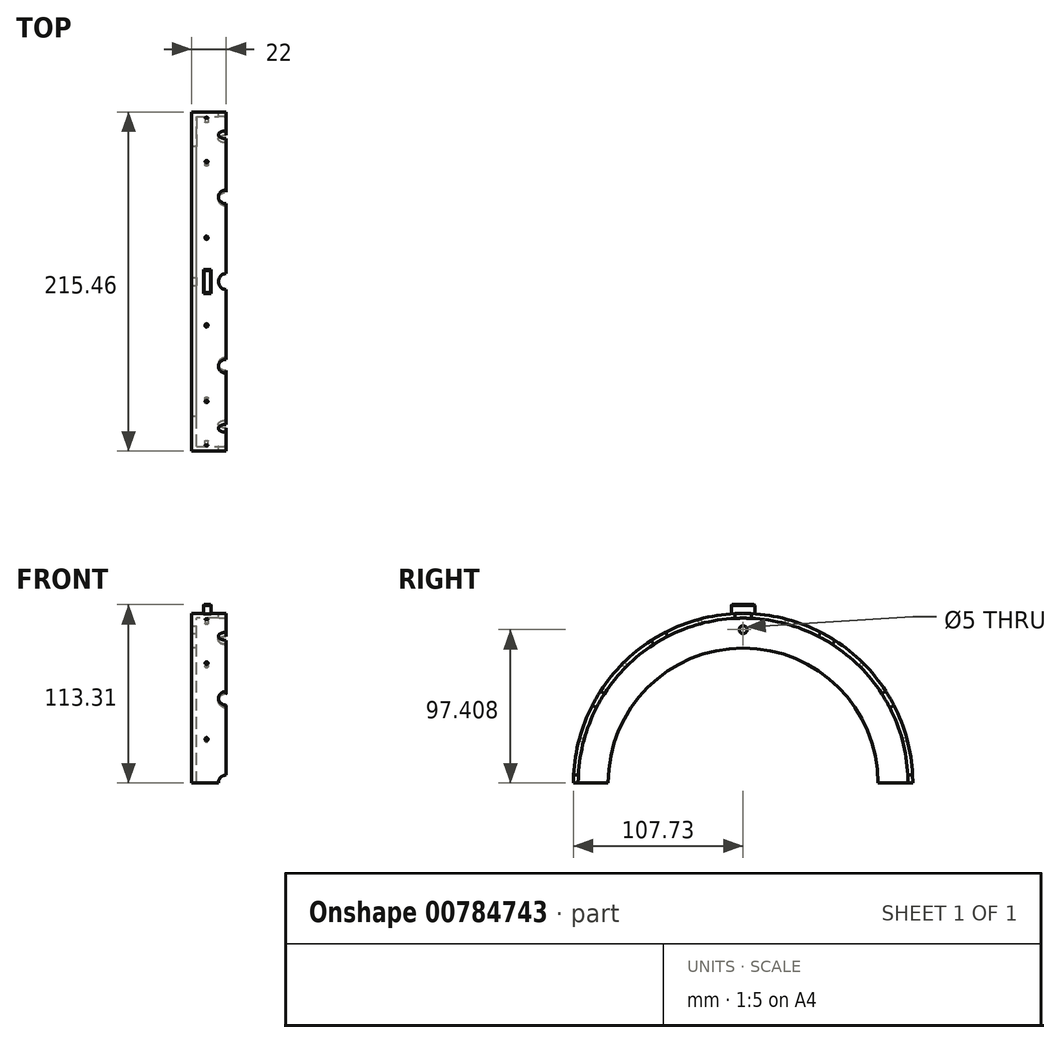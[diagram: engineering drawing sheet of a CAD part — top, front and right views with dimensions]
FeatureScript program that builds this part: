
annotation { "Feature Type Name" : "Feature", "Feature Type Description" : "" }
export const myFeature = defineFeature(function(context is Context, id is Id, definition is map)
    precondition{}
    {
        {
            var Q0;
            Q0=qCreatedBy(makeId("Top.planeOp"),FACE);
            var sketch = newSketch(context, id + "F0", { "sketchPlane" : qUnion([Q0])});
            skLineSegment(sketch, "E0", {"start": v(-37.45, 0) * mm, "end": v(31.85, 0) * mm, "construction": true});
            skLineSegment(sketch, "E1", {"start": v(-6.93, 104.73) * mm, "end": v(-6.93, 85.73) * mm});
            skLineSegment(sketch, "E2", {"start": v(-6.93, 85.73) * mm, "end": v(-9.93, 85.73) * mm});
            skLineSegment(sketch, "E3", {"start": v(-9.93, 85.73) * mm, "end": v(-9.93, 107.73) * mm});
            skLineSegment(sketch, "E4", {"start": v(-6.93, 104.73) * mm, "end": v(9.07, 104.73) * mm});
            skLineSegment(sketch, "E5", {"start": v(12.07, 107.73) * mm, "end": v(12.07, 104.73) * mm});
            skLineSegment(sketch, "E6", {"start": v(-9.93, 107.73) * mm, "end": v(12.07, 107.73) * mm});
            skLineSegment(sketch, "E7.trimOffspring", {"start": v(10.07, 104.73) * mm, "end": v(12.07, 104.73) * mm});
            skLineSegment(sketch, "E8", {"start": v(9.07, 104.73) * mm, "end": v(10.07, 104.73) * mm});
            skSolve(sketch);
        }
        {
            var Q0;
            Q0=qSketchRegion(id+"F0",true);
            var Q1;
            Q1=sQuery(id+"F0.wireOp",EDGE,"E0");
            revolve(context, id + "F1", {"surfaceOperationType" : NewSurfaceOperationType.NEW, "entities" : qUnion([Q0]), "axis" : qUnion([Q1]), "revolveType" : RevolveType.ONE_DIRECTION, "angle" : 180 * degree});
        }
        {
            var Q0;
            Q0=qCreatedBy(makeId("Right.planeOp"),FACE);
            var sketch = newSketch(context, id + "F2", { "sketchPlane" : qUnion([Q0])});
            skLineSegment(sketch, "E9", {"start": v(0, 0) * mm, "end": v(61.84, 107.11) * mm, "construction": true});
            skLineSegment(sketch, "E10", {"start": v(0, 0) * mm, "end": v(0, 110.2) * mm, "construction": true});
            skLineSegment(sketch, "E11", {"start": v(0, 0) * mm, "end": v(-59.27, 102.65) * mm, "construction": true});
            skLineSegment(sketch, "E12", {"start": v(0, 0) * mm, "end": v(108.53, 62.66) * mm, "construction": true});
            skLineSegment(sketch, "E13", {"start": v(0, 0) * mm, "end": v(-111.98, 64.65) * mm, "construction": true});
            skLineSegment(sketch, "E14", {"start": v(0, 0) * mm, "end": v(-132.1, 0) * mm, "construction": true});
            skLineSegment(sketch, "E15", {"start": v(0, 0) * mm, "end": v(126.53, 0) * mm, "construction": true});
            skPoint(sketch, "E16", {"position": v(-59.27, 102.65) * mm});
            skPoint(sketch, "E17", {"position": v(-111.98, 64.65) * mm});
            skPoint(sketch, "E18", {"position": v(-132.1, 0) * mm});
            skPoint(sketch, "E19", {"position": v(0, 110.2) * mm});
            skPoint(sketch, "E20", {"position": v(61.84, 107.11) * mm});
            skPoint(sketch, "E21", {"position": v(108.53, 62.66) * mm});
            skPoint(sketch, "E22", {"position": v(126.53, 0) * mm});
            skLineSegment(sketch, "E23", {"start": v(0, 0) * mm, "end": v(-120.74, 32.35) * mm, "construction": true});
            skLineSegment(sketch, "E24.MirrorCS", {"start": v(0, 0) * mm, "end": v(-88.39, 88.39) * mm, "construction": true});
            skLineSegment(sketch, "E25.MirrorCS", {"start": v(0, 0) * mm, "end": v(-32.35, 120.74) * mm, "construction": true});
            skLineSegment(sketch, "E26.MirrorCS", {"start": v(0, 0) * mm, "end": v(32.35, 120.74) * mm, "construction": true});
            skLineSegment(sketch, "E27.MirrorCS", {"start": v(0, 0) * mm, "end": v(88.39, 88.39) * mm, "construction": true});
            skLineSegment(sketch, "E28.MirrorCS", {"start": v(0, 0) * mm, "end": v(120.74, 32.35) * mm, "construction": true});
            skSolve(sketch);
        }
        {
            var Q0;
            Q0=qCreatedBy(makeId("Front.planeOp"),FACE);
            var Q1;
            Q1=sQuery(id+"F2.wireOp",EDGE,"E13");
            cPlane(context, id + "F3", {"entities" : qUnion([Q0, Q1]), "cplaneType" : CPlaneType.LINE_ANGLE, "offset" : 25 * mm, "angle" : 0 * degree, "width" : 150 * mm, "height" : 150 * mm});
        }
        {
            var Q0;
            Q0=qCreatedBy(id+"F3.planeOp",FACE);
            var sketch = newSketch(context, id + "F4", { "sketchPlane" : qUnion([Q0])});
            skArc(sketch, "E29", {"start": v(12.07, -113.43) * mm, "mid": v(17.27, -105.94) * mm, "end": v(12.07, -98.44) * mm});
            skLineSegment(sketch, "E30", {"start": v(12.07, -113.43) * mm, "end": v(12.07, -98.44) * mm});
            skSolve(sketch);
        }
        {
            var Q0;
            Q0=qSketchRegion(id+"F4",true);
            var Q1;
            Q1=sQuery(id+"F4.wireOp",EDGE,"E30");
            revolve(context, id + "F5", {"operationType" : NewBodyOperationType.REMOVE, "surfaceOperationType" : NewSurfaceOperationType.NEW, "entities" : qUnion([Q0]), "axis" : qUnion([Q1]), "revolveType" : RevolveType.FULL, "oppositeDirection" : true});
        }
        {
            var Q0;
            Q0=sQuery(id+"F2.wireOp",EDGE,"E11");
            cPlane(context, id + "F6", {"entities" : qUnion([Q0]), "cplaneType" : CPlaneType.LINE_ANGLE, "offset" : 25 * mm, "angle" : 90 * degree, "width" : 150 * mm, "height" : 150 * mm});
        }
        {
            var Q0;
            Q0=qCreatedBy(id+"F6.planeOp",FACE);
            var sketch = newSketch(context, id + "F7", { "sketchPlane" : qUnion([Q0])});
            skArc(sketch, "E31", {"start": v(-12.1, 98.77) * mm, "mid": v(-6.9, 106.26) * mm, "end": v(-12.1, 113.76) * mm});
            skLineSegment(sketch, "E32", {"start": v(-12.1, 98.77) * mm, "end": v(-12.1, 113.76) * mm});
            skSolve(sketch);
        }
        {
            var Q0;
            Q0=qSketchRegion(id+"F7",true);
            var Q1;
            Q1=sQuery(id+"F7.wireOp",EDGE,"E32");
            revolve(context, id + "F8", {"operationType" : NewBodyOperationType.REMOVE, "surfaceOperationType" : NewSurfaceOperationType.NEW, "entities" : qUnion([Q0]), "axis" : qUnion([Q1]), "revolveType" : RevolveType.FULL, "oppositeDirection" : true});
        }
        {
            var Q0;
            Q0=sQuery(id+"F2.wireOp",EDGE,"E10");
            cPlane(context, id + "F9", {"entities" : qUnion([Q0]), "cplaneType" : CPlaneType.LINE_ANGLE, "offset" : 25 * mm, "angle" : 90 * degree, "width" : 150 * mm, "height" : 150 * mm});
        }
        {
            var Q0;
            Q0=qCreatedBy(id+"F9.planeOp",FACE);
            var sketch = newSketch(context, id + "F10", { "sketchPlane" : qUnion([Q0])});
            skArc(sketch, "E33", {"start": v(-12.07, 98.66) * mm, "mid": v(-6.87, 106.16) * mm, "end": v(-12.07, 113.65) * mm});
            skLineSegment(sketch, "E34", {"start": v(-12.07, 98.66) * mm, "end": v(-12.07, 113.65) * mm});
            skSolve(sketch);
        }
        {
            var Q0;
            Q0=qSketchRegion(id+"F10",true);
            var Q1;
            Q1=sQuery(id+"F10.wireOp",EDGE,"E34");
            revolve(context, id + "F11", {"operationType" : NewBodyOperationType.REMOVE, "surfaceOperationType" : NewSurfaceOperationType.NEW, "entities" : qUnion([Q0]), "axis" : qUnion([Q1]), "revolveType" : RevolveType.FULL, "oppositeDirection" : true});
        }
        {
            var Q0;
            Q0=sQuery(id+"F2.wireOp",EDGE,"E9");
            cPlane(context, id + "F12", {"entities" : qUnion([Q0]), "cplaneType" : CPlaneType.LINE_ANGLE, "offset" : 25 * mm, "angle" : 90 * degree, "width" : 150 * mm, "height" : 150 * mm});
        }
        {
            var Q0;
            Q0=qCreatedBy(id+"F12.planeOp",FACE);
            var sketch = newSketch(context, id + "F13", { "sketchPlane" : qUnion([Q0])});
            skArc(sketch, "E35", {"start": v(-12.07, 98.61) * mm, "mid": v(-6.87, 106.1) * mm, "end": v(-12.07, 113.6) * mm});
            skLineSegment(sketch, "E36", {"start": v(-12.07, 98.61) * mm, "end": v(-12.07, 113.6) * mm});
            skSolve(sketch);
        }
        {
            var Q0;
            Q0=qSketchRegion(id+"F13",true);
            var Q1;
            Q1=sQuery(id+"F13.wireOp",EDGE,"E36");
            revolve(context, id + "F14", {"operationType" : NewBodyOperationType.REMOVE, "surfaceOperationType" : NewSurfaceOperationType.NEW, "entities" : qUnion([Q0]), "axis" : qUnion([Q1]), "revolveType" : RevolveType.FULL, "oppositeDirection" : true});
        }
        {
            var Q0;
            Q0=sQuery(id+"F2.wireOp",EDGE,"E12");
            cPlane(context, id + "F15", {"entities" : qUnion([Q0]), "cplaneType" : CPlaneType.LINE_ANGLE, "offset" : 25 * mm, "angle" : 0 * degree, "width" : 150 * mm, "height" : 150 * mm});
        }
        {
            var Q0;
            Q0=qCreatedBy(id+"F15.planeOp",FACE);
            var sketch = newSketch(context, id + "F16", { "sketchPlane" : qUnion([Q0])});
            skArc(sketch, "E37", {"start": v(12.07, 98.66) * mm, "mid": v(17.27, 106.16) * mm, "end": v(12.07, 113.65) * mm});
            skLineSegment(sketch, "E38", {"start": v(12.07, 98.66) * mm, "end": v(12.07, 113.65) * mm});
            skSolve(sketch);
        }
        {
            var Q0;
            Q0=qSketchRegion(id+"F16",true);
            var Q1;
            Q1=sQuery(id+"F16.wireOp",EDGE,"E38");
            revolve(context, id + "F17", {"operationType" : NewBodyOperationType.REMOVE, "surfaceOperationType" : NewSurfaceOperationType.NEW, "entities" : qUnion([Q0]), "axis" : qUnion([Q1]), "revolveType" : RevolveType.FULL, "oppositeDirection" : true});
        }
        {
            var Q0;
            Q0=sQuery(id+"F2.wireOp",EDGE,"E23");
            cPlane(context, id + "F18", {"entities" : qUnion([Q0]), "cplaneType" : CPlaneType.LINE_ANGLE, "offset" : 25 * mm, "angle" : 0 * degree, "width" : 150 * mm, "height" : 150 * mm});
        }
        {
            var Q0;
            Q0=sQuery(id+"F2.wireOp",EDGE,"E24.MirrorCS");
            cPlane(context, id + "F19", {"entities" : qUnion([Q0]), "cplaneType" : CPlaneType.LINE_ANGLE, "offset" : 25 * mm, "angle" : 0 * degree, "width" : 150 * mm, "height" : 150 * mm});
        }
        {
            var Q0;
            Q0=sQuery(id+"F2.wireOp",EDGE,"E25.MirrorCS");
            cPlane(context, id + "F20", {"entities" : qUnion([Q0]), "cplaneType" : CPlaneType.LINE_ANGLE, "offset" : 25 * mm, "angle" : 90 * degree, "width" : 150 * mm, "height" : 150 * mm});
        }
        {
            var Q0;
            Q0=sQuery(id+"F2.wireOp",EDGE,"E26.MirrorCS");
            cPlane(context, id + "F21", {"entities" : qUnion([Q0]), "cplaneType" : CPlaneType.LINE_ANGLE, "offset" : 25 * mm, "angle" : 90 * degree, "width" : 150 * mm, "height" : 150 * mm});
        }
        {
            var Q0;
            Q0=sQuery(id+"F2.wireOp",EDGE,"E27.MirrorCS");
            cPlane(context, id + "F22", {"entities" : qUnion([Q0]), "cplaneType" : CPlaneType.LINE_ANGLE, "offset" : 25 * mm, "angle" : 0 * degree, "width" : 150 * mm, "height" : 150 * mm});
        }
        {
            var Q0;
            Q0=sQuery(id+"F2.wireOp",EDGE,"E28.MirrorCS");
            cPlane(context, id + "F23", {"entities" : qUnion([Q0]), "cplaneType" : CPlaneType.LINE_ANGLE, "offset" : 25 * mm, "angle" : 0 * degree, "width" : 150 * mm, "height" : 150 * mm});
        }
        {
            var Q0;
            Q0=qCreatedBy(id+"F18.planeOp",FACE);
            var sketch = newSketch(context, id + "F24", { "sketchPlane" : qUnion([Q0])});
            skLineSegment(sketch, "E39.bottom", {"start": v(-1.5, 110.33) * mm, "end": v(-0.5, 110.33) * mm});
            skLineSegment(sketch, "E39.top", {"start": v(-1.5, 102.33) * mm, "end": v(-0.5, 102.33) * mm});
            skLineSegment(sketch, "E39.left", {"start": v(-1.5, 110.33) * mm, "end": v(-1.5, 102.33) * mm});
            skLineSegment(sketch, "E39.right", {"start": v(-0.5, 110.33) * mm, "end": v(-0.5, 102.33) * mm});
            skSolve(sketch);
        }
        {
            var Q0;
            Q0=qSketchRegion(id+"F24",true);
            var Q1;
            Q1=sQuery(id+"F24.wireOp",EDGE,"E39.right");
            revolve(context, id + "F25", {"operationType" : NewBodyOperationType.REMOVE, "surfaceOperationType" : NewSurfaceOperationType.NEW, "entities" : qUnion([Q0]), "axis" : qUnion([Q1]), "revolveType" : RevolveType.FULL, "oppositeDirection" : true});
        }
        {
            var Q0;
            Q0=qCreatedBy(id+"F19.planeOp",FACE);
            var sketch = newSketch(context, id + "F26", { "sketchPlane" : qUnion([Q0])});
            skLineSegment(sketch, "E40.bottom", {"start": v(-1.5, 111.6) * mm, "end": v(-0.5, 111.6) * mm});
            skLineSegment(sketch, "E40.top", {"start": v(-1.5, 103.6) * mm, "end": v(-0.5, 103.6) * mm});
            skLineSegment(sketch, "E40.left", {"start": v(-1.5, 111.6) * mm, "end": v(-1.5, 103.6) * mm});
            skLineSegment(sketch, "E40.right", {"start": v(-0.5, 111.6) * mm, "end": v(-0.5, 103.6) * mm});
            skSolve(sketch);
        }
        {
            var Q0;
            Q0=qSketchRegion(id+"F26",true);
            var Q1;
            Q1=sQuery(id+"F26.wireOp",EDGE,"E40.right");
            revolve(context, id + "F27", {"operationType" : NewBodyOperationType.REMOVE, "surfaceOperationType" : NewSurfaceOperationType.NEW, "entities" : qUnion([Q0]), "axis" : qUnion([Q1]), "revolveType" : RevolveType.FULL, "oppositeDirection" : true});
        }
        {
            var Q0;
            Q0=qCreatedBy(id+"F20.planeOp",FACE);
            var sketch = newSketch(context, id + "F28", { "sketchPlane" : qUnion([Q0])});
            skLineSegment(sketch, "E41.bottom", {"start": v(0.5, 111.69) * mm, "end": v(1.5, 111.69) * mm});
            skLineSegment(sketch, "E41.top", {"start": v(0.5, 103.69) * mm, "end": v(1.5, 103.69) * mm});
            skLineSegment(sketch, "E41.left", {"start": v(0.5, 111.69) * mm, "end": v(0.5, 103.69) * mm});
            skLineSegment(sketch, "E41.right", {"start": v(1.5, 111.69) * mm, "end": v(1.5, 103.69) * mm});
            skSolve(sketch);
        }
        {
            var Q0;
            Q0=qSketchRegion(id+"F28",true);
            var Q1;
            Q1=sQuery(id+"F28.wireOp",EDGE,"E41.left");
            revolve(context, id + "F29", {"operationType" : NewBodyOperationType.REMOVE, "surfaceOperationType" : NewSurfaceOperationType.NEW, "entities" : qUnion([Q0]), "axis" : qUnion([Q1]), "revolveType" : RevolveType.FULL, "oppositeDirection" : true});
        }
        {
            var Q0;
            Q0=qCreatedBy(id+"F21.planeOp",FACE);
            var sketch = newSketch(context, id + "F30", { "sketchPlane" : qUnion([Q0])});
            skLineSegment(sketch, "E42.bottom", {"start": v(0.5, 112.04) * mm, "end": v(1.5, 112.04) * mm});
            skLineSegment(sketch, "E42.top", {"start": v(0.5, 104.04) * mm, "end": v(1.5, 104.04) * mm});
            skLineSegment(sketch, "E42.left", {"start": v(0.5, 112.04) * mm, "end": v(0.5, 104.04) * mm});
            skLineSegment(sketch, "E42.right", {"start": v(1.5, 112.04) * mm, "end": v(1.5, 104.04) * mm});
            skSolve(sketch);
        }
        {
            var Q0;
            Q0=qSketchRegion(id+"F30",true);
            var Q1;
            Q1=sQuery(id+"F30.wireOp",EDGE,"E42.left");
            revolve(context, id + "F31", {"operationType" : NewBodyOperationType.REMOVE, "surfaceOperationType" : NewSurfaceOperationType.NEW, "entities" : qUnion([Q0]), "axis" : qUnion([Q1]), "revolveType" : RevolveType.FULL, "oppositeDirection" : true});
        }
        {
            var Q0;
            Q0=qCreatedBy(id+"F22.planeOp",FACE);
            var sketch = newSketch(context, id + "F32", { "sketchPlane" : qUnion([Q0])});
            skLineSegment(sketch, "E43.bottom", {"start": v(-1.5, 112) * mm, "end": v(-0.5, 112) * mm});
            skLineSegment(sketch, "E43.top", {"start": v(-1.5, 104) * mm, "end": v(-0.5, 104) * mm});
            skLineSegment(sketch, "E43.left", {"start": v(-1.5, 112) * mm, "end": v(-1.5, 104) * mm});
            skLineSegment(sketch, "E43.right", {"start": v(-0.5, 112) * mm, "end": v(-0.5, 104) * mm});
            skSolve(sketch);
        }
        {
            var Q0;
            Q0=qSketchRegion(id+"F32",true);
            var Q1;
            Q1=sQuery(id+"F32.wireOp",EDGE,"E43.right");
            revolve(context, id + "F33", {"operationType" : NewBodyOperationType.REMOVE, "surfaceOperationType" : NewSurfaceOperationType.NEW, "entities" : qUnion([Q0]), "axis" : qUnion([Q1]), "revolveType" : RevolveType.FULL, "oppositeDirection" : true});
        }
        {
            var Q0;
            Q0=qCreatedBy(id+"F23.planeOp",FACE);
            var sketch = newSketch(context, id + "F34", { "sketchPlane" : qUnion([Q0])});
            skLineSegment(sketch, "E44.bottom", {"start": v(-1.5, 110.24) * mm, "end": v(-0.5, 110.24) * mm});
            skLineSegment(sketch, "E44.top", {"start": v(-1.5, 102.24) * mm, "end": v(-0.5, 102.24) * mm});
            skLineSegment(sketch, "E44.left", {"start": v(-1.5, 110.24) * mm, "end": v(-1.5, 102.24) * mm});
            skLineSegment(sketch, "E44.right", {"start": v(-0.5, 110.24) * mm, "end": v(-0.5, 102.24) * mm});
            skSolve(sketch);
        }
        {
            var Q0;
            Q0=qSketchRegion(id+"F34",true);
            var Q1;
            Q1=sQuery(id+"F34.wireOp",EDGE,"E44.right");
            revolve(context, id + "F35", {"operationType" : NewBodyOperationType.REMOVE, "surfaceOperationType" : NewSurfaceOperationType.NEW, "entities" : qUnion([Q0]), "axis" : qUnion([Q1]), "revolveType" : RevolveType.FULL, "oppositeDirection" : true});
        }
        {
            var Q0;
            Q0=qCreatedBy(makeId("Top.planeOp"),FACE);
            var sketch = newSketch(context, id + "F36", { "sketchPlane" : qUnion([Q0])});
            skArc(sketch, "E45", {"start": v(12.07, 98.74) * mm, "mid": v(17.27, 106.24) * mm, "end": v(12.07, 113.73) * mm});
            skLineSegment(sketch, "E46", {"start": v(12.07, 98.74) * mm, "end": v(12.07, 113.73) * mm});
            skLineSegment(sketch, "E47.MirrorCS", {"start": v(12.07, -98.74) * mm, "end": v(12.07, -113.73) * mm});
            skArc(sketch, "E48.MirrorCS", {"start": v(12.07, -98.74) * mm, "mid": v(17.27, -106.24) * mm, "end": v(12.07, -113.73) * mm});
            skSolve(sketch);
        }
        {
            var Q0;
            Q0=qSketchRegion(id+"F36",true);
            var Q1;
            Q1=sQuery(id+"F36.wireOp",EDGE,"E46");
            revolve(context, id + "F37", {"operationType" : NewBodyOperationType.REMOVE, "surfaceOperationType" : NewSurfaceOperationType.NEW, "entities" : qUnion([Q0]), "axis" : qUnion([Q1]), "revolveType" : RevolveType.ONE_DIRECTION, "oppositeDirection" : true, "angle" : 180 * degree});
        }
        {
            var Q0;
            Q0=qCreatedBy(makeId("Right.planeOp"),FACE);
            var sketch = newSketch(context, id + "F38", { "sketchPlane" : qUnion([Q0])});
            skLineSegment(sketch, "E49", {"start": v(-7.5, 106.3) * mm, "end": v(-7.5, 113.3) * mm});
            skLineSegment(sketch, "E50", {"start": v(-7.5, 113.3) * mm, "end": v(7.5, 113.3) * mm});
            skLineSegment(sketch, "E51", {"start": v(7.5, 113.3) * mm, "end": v(7.5, 106.3) * mm});
            skArc(sketch, "E52", {"start": v(7.5, 106.3) * mm, "mid": v(0, 107.12) * mm, "end": v(-7.5, 106.3) * mm});
            skPoint(sketch, "E53.positionSnap0", {"position": v(0, 107.12) * mm});
            skCircle(sketch, "E54", {"center": v(0, 97.4) * mm, "radius": 2.5 * mm});
            skSolve(sketch);
        }
        {
            var Q0;
            Q0=makeQuery(id+"F38.imprint","IMPRINT",FACE,{"disambiguationData":[TD([[makeQuery(id+"F38.imprint","IMPRINT",EDGE,{"derivedFrom":sQuery(id+"F38.wireOp",EDGE,"E49")}),-1.0]])]});
            extrude(context, id + "F39", {"entities" : qUnion([Q0]), "operationType" : NewBodyOperationType.ADD, "depth" : 5 * mm, "offsetDistance" : 25 * mm, "symmetric" : true});
        }
        {
            var Q0;
            Q0=makeQuery(id+"F39.opExtrude","CAP_EDGE",EDGE,{"disambiguationData":[OSD([sQuery(id+"F38.wireOp",EDGE,"E50")])],"isStart":false});
            var Q1;
            Q1=makeQuery(id+"F39.opExtrude","SWEPT_EDGE",EDGE,{"disambiguationData":[OSD([sQuery(id+"F38.wireOp",EDGE,"E49"),sQuery(id+"F38.wireOp",EDGE,"E50")])]});
            var Q2;
            Q2=makeQuery(id+"F39.opExtrude","CAP_EDGE",EDGE,{"disambiguationData":[OSD([sQuery(id+"F38.wireOp",EDGE,"E50")])],"isStart":true});
            var Q3;
            Q3=makeQuery(id+"F39.opExtrude","SWEPT_EDGE",EDGE,{"disambiguationData":[OSD([sQuery(id+"F38.wireOp",EDGE,"E50"),sQuery(id+"F38.wireOp",EDGE,"E51")])]});
            chamfer(context, id + "F40", {"entities" : qUnion([Q0, Q1, Q2, Q3]), "width" : 0.5 * mm, "tangentPropagation" : true});
        }
        {
            var Q0;
            Q0=makeQuery(id+"F38.imprint","IMPRINT",FACE,{"disambiguationData":[TD([[makeQuery(id+"F38.imprint","IMPRINT",EDGE,{"derivedFrom":sQuery(id+"F38.wireOp",EDGE,"E54")}),1.0]])]});
            extrude(context, id + "F41", {"entities" : qUnion([Q0]), "operationType" : NewBodyOperationType.REMOVE, "oppositeDirection" : true, "depth" : 10 * mm, "offsetDistance" : 25 * mm});
        }
    });
